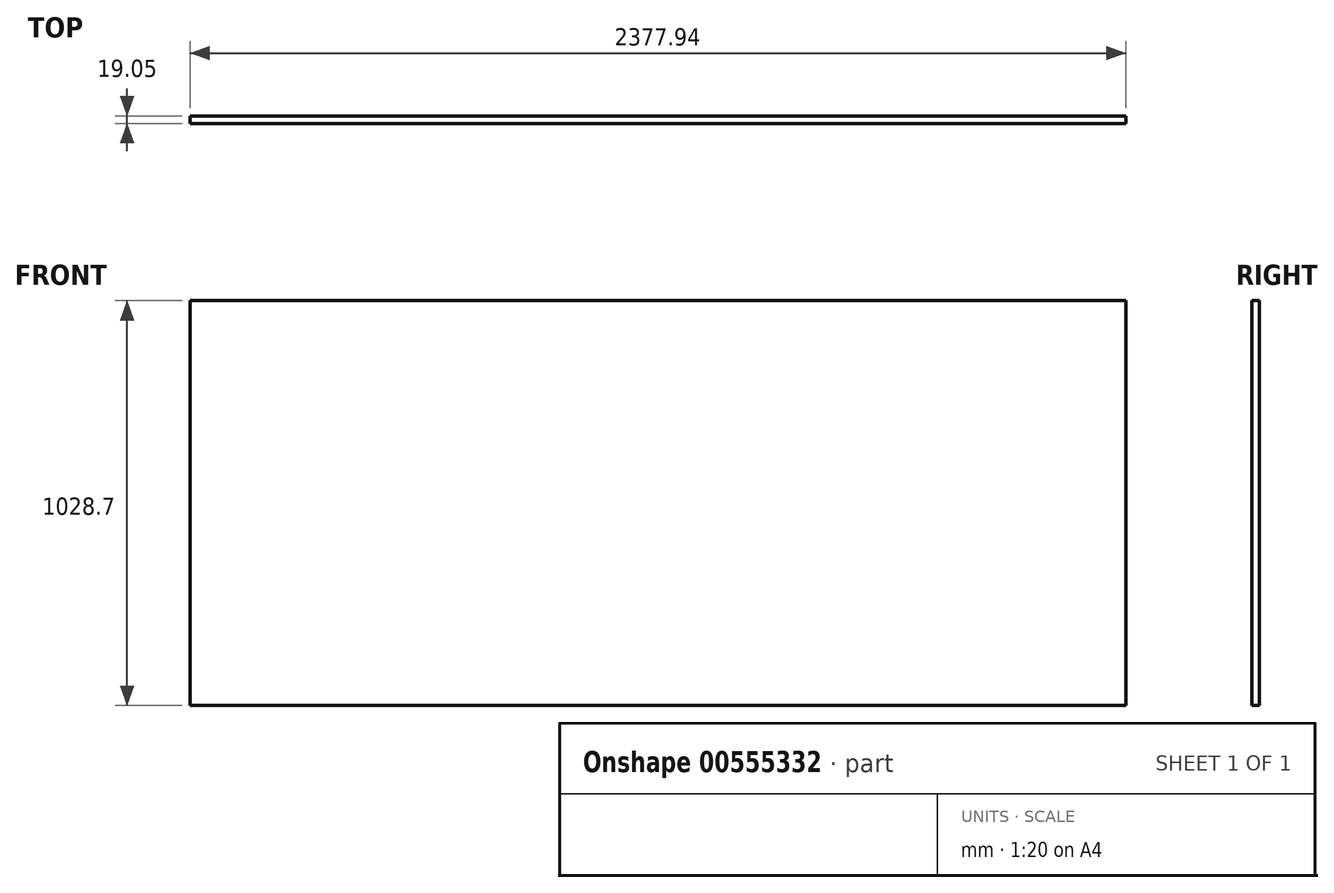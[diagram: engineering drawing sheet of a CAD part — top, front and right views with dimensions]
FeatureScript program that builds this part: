
annotation { "Feature Type Name" : "Feature", "Feature Type Description" : "" }
export const myFeature = defineFeature(function(context is Context, id is Id, definition is map)
    precondition{}
    {
        {
            var Q0;
            Q0=qCreatedBy(makeId("Front.planeOp"),FACE);
            var sketch = newSketch(context, id + "F0", { "sketchPlane" : qUnion([Q0])});
            skLineSegment(sketch, "E0.bottom", {"start": v(1188.97, 514.35) * mm, "end": v(-1188.97, 514.35) * mm});
            skLineSegment(sketch, "E0.top", {"start": v(1188.97, -514.35) * mm, "end": v(-1188.97, -514.35) * mm});
            skLineSegment(sketch, "E0.left", {"start": v(1188.97, 514.35) * mm, "end": v(1188.97, -514.35) * mm});
            skLineSegment(sketch, "E0.right", {"start": v(-1188.97, 514.35) * mm, "end": v(-1188.97, -514.35) * mm});
            skPoint(sketch, "E0.middle", {"position": v(0, 0) * mm});
            skSolve(sketch);
        }
        {
            var Q0;
            Q0=makeQuery(id+"F0.imprint","IMPRINT",FACE,{"disambiguationData":[TD([[makeQuery(id+"F0.imprint","IMPRINT",EDGE,{"derivedFrom":sQuery(id+"F0.wireOp",EDGE,"E0.bottom")}),1.0]])]});
            extrude(context, id + "F1", {"entities" : qUnion([Q0]), "depth" : 19.05 * mm, "offsetDistance" : 25.4 * mm});
        }
    });
